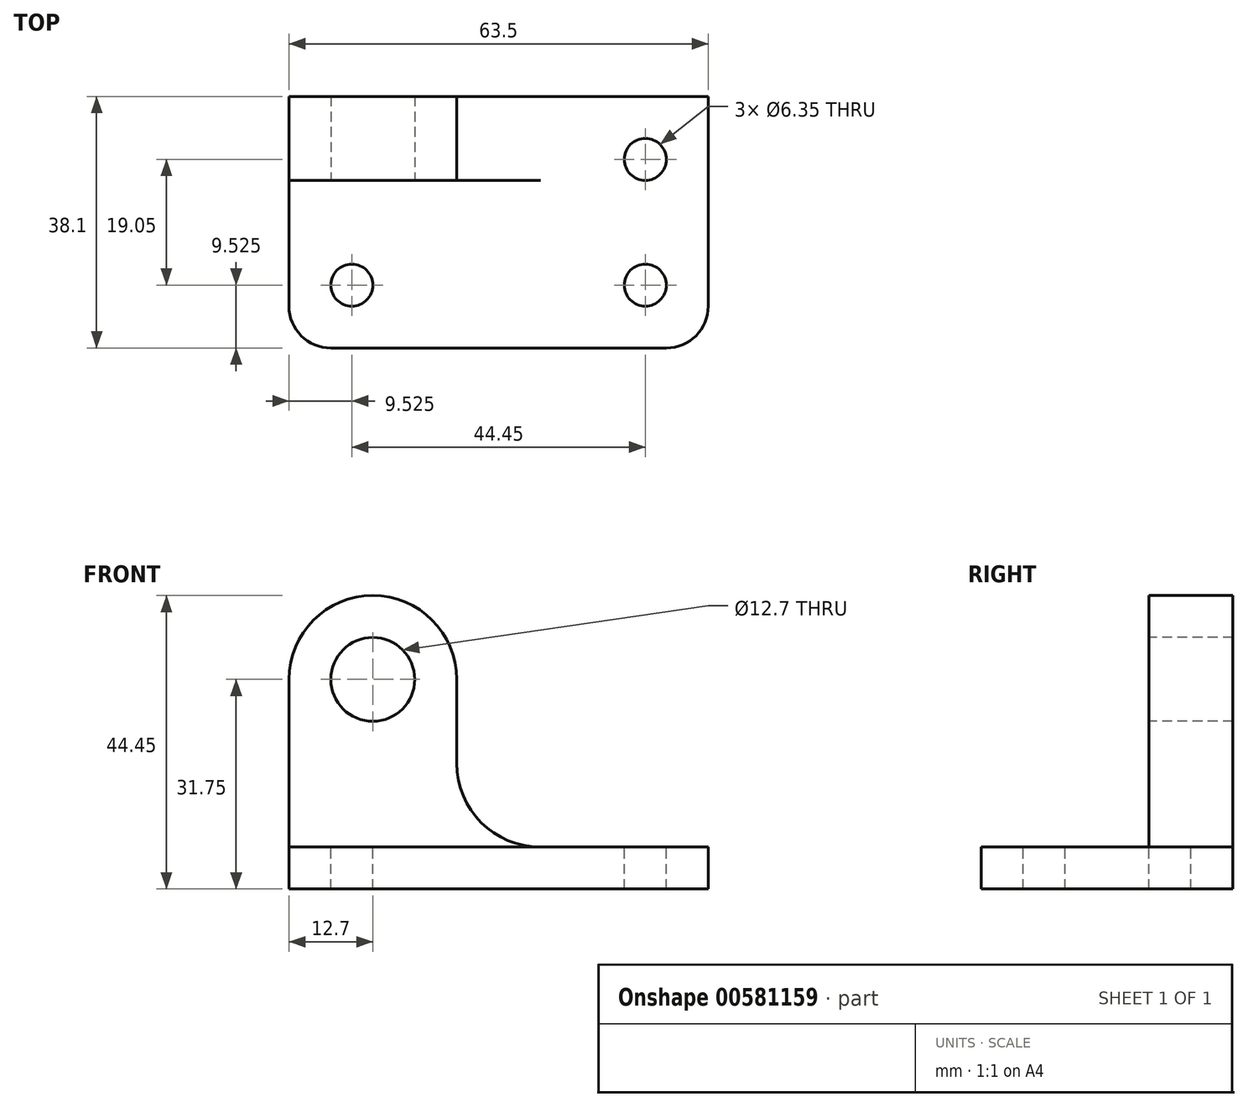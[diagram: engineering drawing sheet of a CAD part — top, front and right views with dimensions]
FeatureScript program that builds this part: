
annotation { "Feature Type Name" : "Feature", "Feature Type Description" : "" }
export const myFeature = defineFeature(function(context is Context, id is Id, definition is map)
    precondition{}
    {
        {
            var Q0;
            Q0=qCreatedBy(makeId("Front.planeOp"),FACE);
            var sketch = newSketch(context, id + "F0", { "sketchPlane" : qUnion([Q0])});
            skLineSegment(sketch, "E0", {"start": v(0, 0) * mm, "end": v(63.5, 0) * mm});
            skLineSegment(sketch, "E1", {"start": v(63.5, 0) * mm, "end": v(63.5, 6.35) * mm});
            skLineSegment(sketch, "E2", {"start": v(63.5, 6.35) * mm, "end": v(38.1, 6.35) * mm});
            skLineSegment(sketch, "E3", {"start": v(38.1, 6.35) * mm, "end": v(38.1, 44.45) * mm});
            skLineSegment(sketch, "E4", {"start": v(38.1, 44.45) * mm, "end": v(0, 44.45) * mm});
            skLineSegment(sketch, "E5", {"start": v(0, 44.45) * mm, "end": v(0, 0) * mm});
            skSolve(sketch);
        }
        {
            var Q0;
            Q0=makeQuery(id+"F0.imprint","IMPRINT",FACE,{"disambiguationData":[TD([[makeQuery(id+"F0.imprint","IMPRINT",EDGE,{"derivedFrom":sQuery(id+"F0.wireOp",EDGE,"E0")}),1.0]])]});
            extrude(context, id + "F1", {"entities" : qUnion([Q0]), "depth" : 38.1 * mm, "offsetDistance" : 25.4 * mm});
        }
        {
            var Q0;
            Q0=makeQuery(id+"F1.opExtrude","SWEPT_FACE",FACE,{"disambiguationData":[OSD([sQuery(id+"F0.wireOp",EDGE,"E4")])]});
            var sketch = newSketch(context, id + "F2", { "sketchPlane" : qUnion([Q0])});
            skLineSegment(sketch, "E6", {"start": v(0, -12.7) * mm, "end": v(38.1, -12.7) * mm});
            skSolve(sketch);
        }
        {
            var Q0;
            {var subQ0=sQuery(id+"F2.wireOp",EDGE,"E6");Q0=makeQuery(id+"F2.imprint","IMPRINT",FACE,{"disambiguationData":[TD([[makeQuery(id+"F2.imprint","IMPRINT",EDGE,{"derivedFrom":subQ0}),-1.0]])]});}
            extrude(context, id + "F3", {"entities" : qUnion([Q0]), "operationType" : NewBodyOperationType.REMOVE, "oppositeDirection" : true, "depth" : 38.1 * mm, "offsetDistance" : 25.4 * mm});
        }
        {
            var Q0;
            Q0=makeQuery(id+"F3.boolean.opBoolean","MERGE",FACE,{"derivedFrom":[makeQuery(id+"F1.opExtrude","SWEPT_FACE",FACE,{"disambiguationData":[OSD([sQuery(id+"F0.wireOp",EDGE,"E2")])]}),makeQuery(id+"F3.opExtrude","CAP_FACE",FACE,{"disambiguationData":[OSD([sQuery(id+"F0.wireOp",EDGE,"E3"),sQuery(id+"F0.wireOp",EDGE,"E4"),sQuery(id+"F0.wireOp",EDGE,"E5"),sQuery(id+"F2.wireOp",EDGE,"E6")])],"isStart":false})]});
            var sketch = newSketch(context, id + "F4", { "sketchPlane" : qUnion([Q0])});
            skCircle(sketch, "E7", {"center": v(53.98, -9.52) * mm, "radius": 3.18 * mm});
            skCircle(sketch, "E8", {"center": v(53.98, -28.58) * mm, "radius": 3.18 * mm});
            skCircle(sketch, "E9", {"center": v(9.53, -28.58) * mm, "radius": 3.18 * mm});
            skSolve(sketch);
        }
        {
            var Q0;
            Q0=makeQuery(id+"F4.imprint","IMPRINT",FACE,{"disambiguationData":[TD([[makeQuery(id+"F4.imprint","IMPRINT",EDGE,{"derivedFrom":sQuery(id+"F4.wireOp",EDGE,"E7")}),1.0]])]});
            var Q1;
            Q1=makeQuery(id+"F4.imprint","IMPRINT",FACE,{"disambiguationData":[TD([[makeQuery(id+"F4.imprint","IMPRINT",EDGE,{"derivedFrom":sQuery(id+"F4.wireOp",EDGE,"E8")}),1.0]])]});
            var Q2;
            Q2=makeQuery(id+"F4.imprint","IMPRINT",FACE,{"disambiguationData":[TD([[makeQuery(id+"F4.imprint","IMPRINT",EDGE,{"derivedFrom":sQuery(id+"F4.wireOp",EDGE,"E9")}),1.0]])]});
            extrude(context, id + "F5", {"entities" : qUnion([Q0, Q1, Q2]), "operationType" : NewBodyOperationType.REMOVE, "oppositeDirection" : true, "depth" : 6.35 * mm, "offsetDistance" : 25.4 * mm});
        }
        {
            var Q0;
            Q0=makeQuery(id+"F1.opExtrude","SWEPT_FACE",FACE,{"disambiguationData":[OSD([sQuery(id+"F0.wireOp",EDGE,"E4")])]});
            var sketch = newSketch(context, id + "F6", { "sketchPlane" : qUnion([Q0])});
            skLineSegment(sketch, "E10", {"start": v(25.4, 0) * mm, "end": v(25.4, -12.7) * mm});
            skSolve(sketch);
        }
        {
            var Q0;
            {var subQ0=sQuery(id+"F6.wireOp",EDGE,"E10");Q0=makeQuery(id+"F6.imprint","IMPRINT",FACE,{"disambiguationData":[TD([[makeQuery(id+"F6.imprint","IMPRINT",EDGE,{"derivedFrom":subQ0}),1.0]])]});}
            extrude(context, id + "F7", {"entities" : qUnion([Q0]), "operationType" : NewBodyOperationType.REMOVE, "oppositeDirection" : true, "depth" : 38.1 * mm, "offsetDistance" : 25.4 * mm});
        }
        {
            var Q0;
            Q0=makeQuery(id+"F3.boolean.opBoolean","COPY",FACE,{"derivedFrom":makeQuery(id+"F3.opExtrude","SWEPT_FACE",FACE,{"disambiguationData":[OSD([sQuery(id+"F2.wireOp",EDGE,"E6")])]})});
            var sketch = newSketch(context, id + "F8", { "sketchPlane" : qUnion([Q0])});
            skCircle(sketch, "E11", {"center": v(12.7, 31.75) * mm, "radius": 6.35 * mm});
            skArc(sketch, "E12", {"start": v(25.4, 31.75) * mm, "mid": v(12.7, 44.45) * mm, "end": v(0, 31.75) * mm});
            skSolve(sketch);
        }
        {
            var Q0;
            Q0=makeQuery(id+"F8.imprint","IMPRINT",FACE,{"disambiguationData":[TD([[makeQuery(id+"F8.imprint","IMPRINT",EDGE,{"derivedFrom":sQuery(id+"F8.wireOp",EDGE,"E11")}),1.0]])]});
            var Q1;
            {var subQ0=sQuery(id+"F8.wireOp",EDGE,"E12");var subQ1=sQuery(id+"F2.wireOp",EDGE,"E6");var subQ4=makeQuery(id+"F3.boolean.opBoolean","COPY",EDGE,{"derivedFrom":makeQuery(id+"F3.opExtrude","CAP_EDGE",EDGE,{"disambiguationData":[OSD([subQ1])],"isStart":true})});var subQ5=makeQuery(id+"F8.imprint","INTERSECT",VERTEX,{"derivedFrom":[subQ4,subQ0]});Q1=makeQuery(id+"F8.imprint","IMPRINT",FACE,{"disambiguationData":[TD([[makeQuery(id+"F8.imprint","IMPRINT",EDGE,{"disambiguationData":[TD([[subQ5,1.0]])],"derivedFrom":subQ0}),-1.0]])]});}
            var Q2;
            {var subQ0=sQuery(id+"F8.wireOp",EDGE,"E12");var subQ1=sQuery(id+"F2.wireOp",EDGE,"E6");var subQ4=makeQuery(id+"F3.boolean.opBoolean","COPY",EDGE,{"derivedFrom":makeQuery(id+"F3.opExtrude","CAP_EDGE",EDGE,{"disambiguationData":[OSD([subQ1])],"isStart":true})});var subQ5=makeQuery(id+"F8.imprint","INTERSECT",VERTEX,{"derivedFrom":[subQ4,subQ0]});Q2=makeQuery(id+"F8.imprint","IMPRINT",FACE,{"disambiguationData":[TD([[makeQuery(id+"F8.imprint","IMPRINT",EDGE,{"disambiguationData":[TD([[subQ5,-1.0]])],"derivedFrom":subQ0}),-1.0]])]});}
            extrude(context, id + "F9", {"entities" : qUnion([Q0, Q1, Q2]), "operationType" : NewBodyOperationType.REMOVE, "oppositeDirection" : true, "depth" : 12.7 * mm, "offsetDistance" : 25.4 * mm});
        }
        {
            var Q0;
            Q0=makeQuery(id+"F7.boolean.opBoolean","COPY",FACE,{"derivedFrom":makeQuery(id+"F7.opExtrude","SWEPT_FACE",FACE,{"disambiguationData":[OSD([sQuery(id+"F6.wireOp",EDGE,"E10")])]})});
            var sketch = newSketch(context, id + "F10", { "sketchPlane" : qUnion([Q0])});
            skLineSegment(sketch, "E13", {"start": v(-12.7, 6.35) * mm, "end": v(0, 6.35) * mm});
            skLineSegment(sketch, "E14", {"start": v(0, 6.35) * mm, "end": v(0, 19.05) * mm});
            skLineSegment(sketch, "E15", {"start": v(0, 19.05) * mm, "end": v(-12.7, 19.05) * mm});
            skLineSegment(sketch, "E16", {"start": v(-12.7, 19.05) * mm, "end": v(-12.7, 6.35) * mm});
            skSolve(sketch);
        }
        {
            var Q0;
            Q0=makeQuery(id+"F10.imprint","IMPRINT",FACE,{"disambiguationData":[TD([[makeQuery(id+"F10.imprint","IMPRINT",EDGE,{"derivedFrom":sQuery(id+"F10.wireOp",EDGE,"E13")}),-1.0]])]});
            extrude(context, id + "F11", {"entities" : qUnion([Q0]), "operationType" : NewBodyOperationType.ADD, "depth" : 12.7 * mm, "offsetDistance" : 25.4 * mm});
        }
        {
            var Q0;
            Q0=makeQuery(id+"F11.boolean.opBoolean","MERGE",FACE,{"derivedFrom":[makeQuery(id+"F3.boolean.opBoolean","COPY",FACE,{"derivedFrom":makeQuery(id+"F3.opExtrude","SWEPT_FACE",FACE,{"disambiguationData":[OSD([sQuery(id+"F2.wireOp",EDGE,"E6")])]})}),makeQuery(id+"F11.opExtrude","SWEPT_FACE",FACE,{"disambiguationData":[OSD([sQuery(id+"F10.wireOp",EDGE,"E16")])]})]});
            var sketch = newSketch(context, id + "F12", { "sketchPlane" : qUnion([Q0])});
            skArc(sketch, "E17", {"start": v(25.4, 19.05) * mm, "mid": v(29.12, 10.07) * mm, "end": v(38.1, 6.35) * mm});
            skSolve(sketch);
        }
        {
            var Q0;
            Q0=makeQuery(id+"F12.imprint","IMPRINT",FACE,{"disambiguationData":[TD([[makeQuery(id+"F12.imprint","IMPRINT",EDGE,{"derivedFrom":sQuery(id+"F12.wireOp",EDGE,"E17")}),1.0]])]});
            extrude(context, id + "F13", {"entities" : qUnion([Q0]), "operationType" : NewBodyOperationType.REMOVE, "oppositeDirection" : true, "depth" : 12.7 * mm, "offsetDistance" : 25.4 * mm});
        }
        {
            var Q0;
            {var subQ0=sQuery(id+"F2.wireOp",EDGE,"E6");var subQ1=sQuery(id+"F0.wireOp",EDGE,"E4");var subQ2=sQuery(id+"F0.wireOp",EDGE,"E3");Q0=makeQuery(id+"F7.boolean.opBoolean","MERGE",FACE,{"derivedFrom":[makeQuery(id+"F3.boolean.opBoolean","MERGE",FACE,{"derivedFrom":[makeQuery(id+"F1.opExtrude","SWEPT_FACE",FACE,{"disambiguationData":[OSD([sQuery(id+"F0.wireOp",EDGE,"E2")])]}),makeQuery(id+"F3.opExtrude","CAP_FACE",FACE,{"disambiguationData":[OSD([subQ2,subQ1,sQuery(id+"F0.wireOp",EDGE,"E5"),subQ0])],"isStart":false})]}),makeQuery(id+"F7.opExtrude","CAP_FACE",FACE,{"disambiguationData":[OSD([subQ2,subQ1,subQ0,sQuery(id+"F6.wireOp",EDGE,"E10")])],"isStart":false})]});}
            var sketch = newSketch(context, id + "F14", { "sketchPlane" : qUnion([Q0])});
            skArc(sketch, "E18", {"start": v(57.15, -38.1) * mm, "mid": v(61.64, -36.24) * mm, "end": v(63.5, -31.75) * mm});
            skArc(sketch, "E19", {"start": v(0, -31.75) * mm, "mid": v(1.86, -36.24) * mm, "end": v(6.35, -38.1) * mm});
            skSolve(sketch);
        }
        {
            var Q0;
            {var subQ0=sQuery(id+"F14.wireOp",EDGE,"E18");Q0=makeQuery(id+"F14.imprint","IMPRINT",FACE,{"disambiguationData":[TD([[makeQuery(id+"F14.imprint","IMPRINT",EDGE,{"derivedFrom":subQ0}),-1.0]])]});}
            var Q1;
            {var subQ0=sQuery(id+"F14.wireOp",EDGE,"E19");Q1=makeQuery(id+"F14.imprint","IMPRINT",FACE,{"disambiguationData":[TD([[makeQuery(id+"F14.imprint","IMPRINT",EDGE,{"derivedFrom":subQ0}),-1.0]])]});}
            extrude(context, id + "F15", {"entities" : qUnion([Q0, Q1]), "operationType" : NewBodyOperationType.REMOVE, "oppositeDirection" : true, "depth" : 6.35 * mm, "offsetDistance" : 25.4 * mm});
        }
    });
